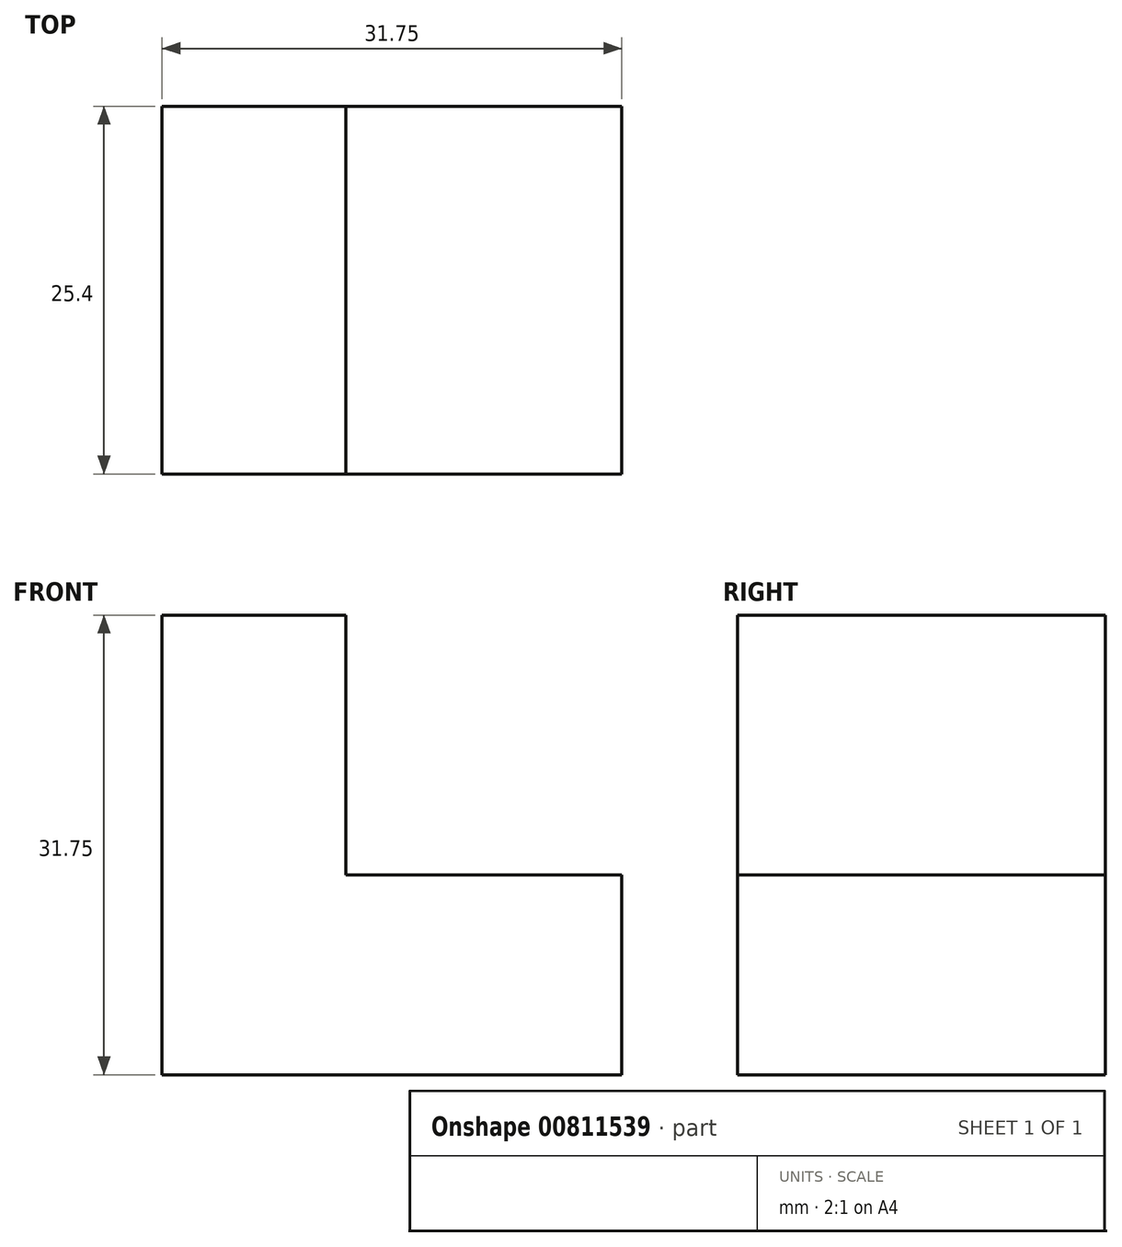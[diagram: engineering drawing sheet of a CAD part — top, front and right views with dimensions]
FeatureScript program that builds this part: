
annotation { "Feature Type Name" : "Feature", "Feature Type Description" : "" }
export const myFeature = defineFeature(function(context is Context, id is Id, definition is map)
    precondition{}
    {
        {
            var Q0;
            Q0=qCreatedBy(makeId("Front.planeOp"),FACE);
            var sketch = newSketch(context, id + "F0", { "sketchPlane" : qUnion([Q0])});
            skLineSegment(sketch, "E0", {"start": v(0, 0) * mm, "end": v(0, 31.75) * mm});
            skLineSegment(sketch, "E1", {"start": v(0, 31.75) * mm, "end": v(12.7, 31.75) * mm});
            skLineSegment(sketch, "E2", {"start": v(12.7, 31.75) * mm, "end": v(12.7, 13.8) * mm});
            skLineSegment(sketch, "E3", {"start": v(12.7, 13.8) * mm, "end": v(31.75, 13.8) * mm});
            skLineSegment(sketch, "E4", {"start": v(31.75, 13.8) * mm, "end": v(31.75, 0) * mm});
            skLineSegment(sketch, "E5", {"start": v(31.75, 0) * mm, "end": v(0, 0) * mm});
            skSolve(sketch);
        }
        {
            var Q0;
            Q0=makeQuery(id+"F0.imprint","IMPRINT",FACE,{"disambiguationData":[TD([[makeQuery(id+"F0.imprint","IMPRINT",EDGE,{"derivedFrom":sQuery(id+"F0.wireOp",EDGE,"E0")}),-1.0]])]});
            extrude(context, id + "F1", {"entities" : qUnion([Q0]), "depth" : 25.4 * mm, "offsetDistance" : 25.4 * mm});
        }
    });
